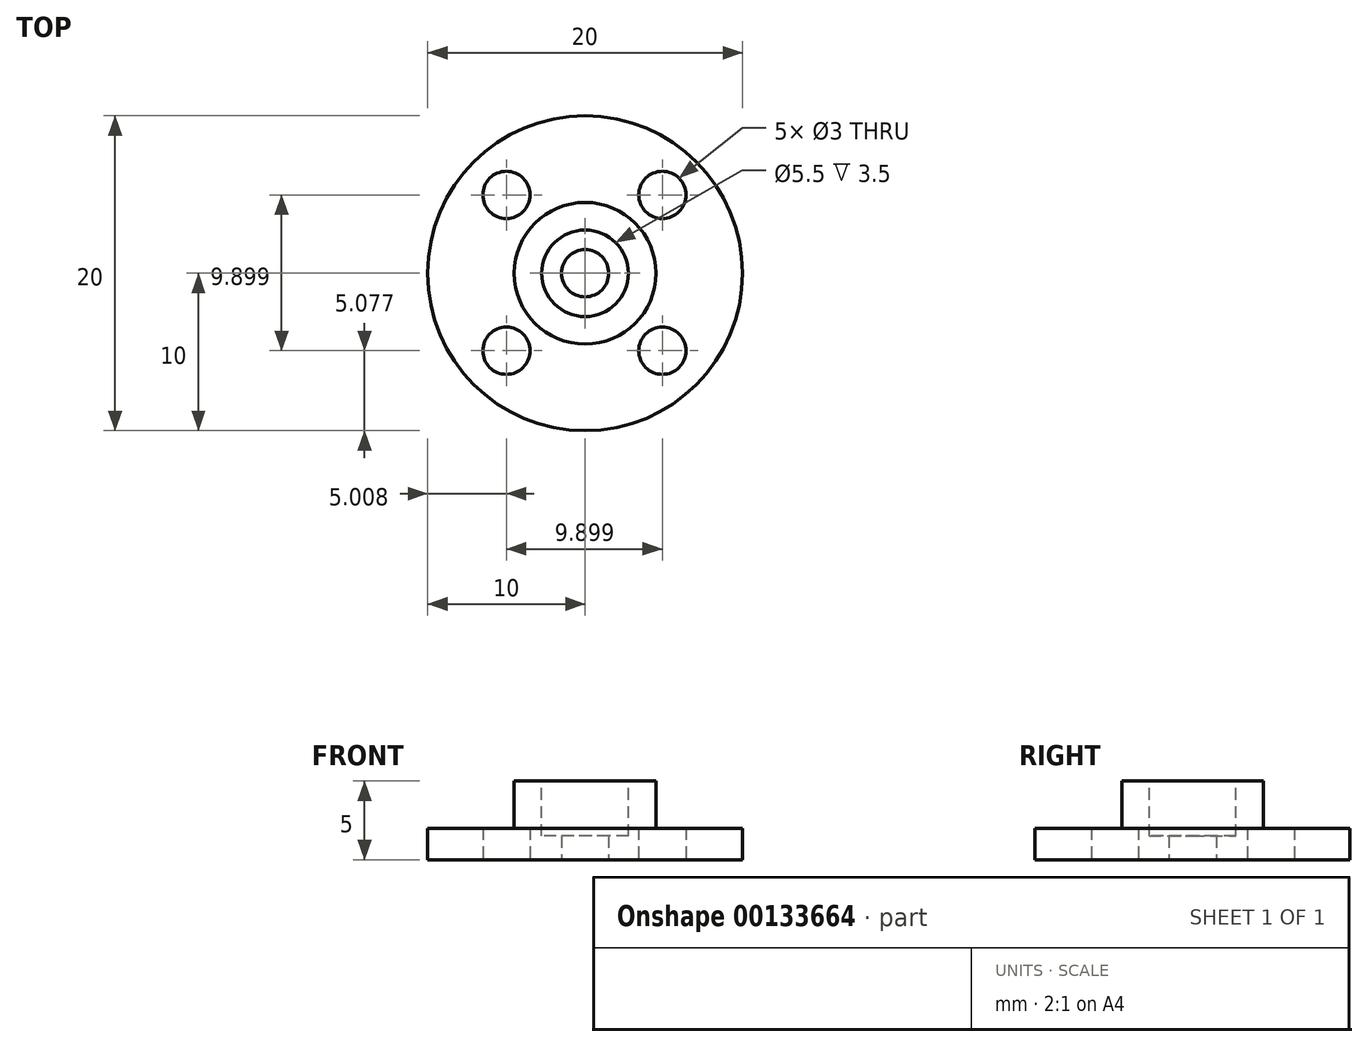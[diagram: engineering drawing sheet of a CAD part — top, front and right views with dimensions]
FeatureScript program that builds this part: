
annotation { "Feature Type Name" : "Feature", "Feature Type Description" : "" }
export const myFeature = defineFeature(function(context is Context, id is Id, definition is map)
    precondition{}
    {
        {
            var Q0;
            Q0=qCreatedBy(makeId("Top.planeOp"),FACE);
            var sketch = newSketch(context, id + "F0", { "sketchPlane" : qUnion([Q0])});
            skCircle(sketch, "E0", {"center": v(0, 0) * mm, "radius": 10 * mm});
            skCircle(sketch, "E1", {"center": v(0, 0) * mm, "radius": 1.5 * mm});
            skLineSegment(sketch, "E2.bottom", {"start": v(-5, -4.92) * mm, "end": v(4.9, -4.92) * mm, "construction": true});
            skLineSegment(sketch, "E2.top", {"start": v(-5, 4.98) * mm, "end": v(4.9, 4.98) * mm, "construction": true});
            skLineSegment(sketch, "E2.left", {"start": v(-5, -4.92) * mm, "end": v(-5, 4.98) * mm, "construction": true});
            skLineSegment(sketch, "E2.right", {"start": v(4.9, -4.92) * mm, "end": v(4.9, 4.98) * mm, "construction": true});
            skPoint(sketch, "E2.middle", {"position": v(-0.04, 0.03) * mm});
            skCircle(sketch, "E3", {"center": v(-5, 4.98) * mm, "radius": 1.5 * mm});
            skCircle(sketch, "E4", {"center": v(4.9, 4.98) * mm, "radius": 1.5 * mm});
            skCircle(sketch, "E5", {"center": v(4.9, -4.92) * mm, "radius": 1.5 * mm});
            skCircle(sketch, "E6", {"center": v(-5, -4.92) * mm, "radius": 1.5 * mm});
            skSolve(sketch);
        }
        {
            var Q0;
            Q0=makeQuery(id+"F0.imprint","IMPRINT",FACE,{"disambiguationData":[TD([[makeQuery(id+"F0.imprint","IMPRINT",EDGE,{"derivedFrom":sQuery(id+"F0.wireOp",EDGE,"E0")}),1.0]])]});
            extrude(context, id + "F1", {"entities" : qUnion([Q0]), "depth" : 2 * mm, "offsetDistance" : 25 * mm});
        }
        {
            var Q0;
            Q0=makeQuery(id+"F1.opExtrude","CAP_FACE",FACE,{"disambiguationData":[OSD([sQuery(id+"F0.wireOp",EDGE,"E0"),sQuery(id+"F0.wireOp",EDGE,"E1"),sQuery(id+"F0.wireOp",EDGE,"E3"),sQuery(id+"F0.wireOp",EDGE,"E4"),sQuery(id+"F0.wireOp",EDGE,"E5"),sQuery(id+"F0.wireOp",EDGE,"E6")])],"isStart":false});
            var sketch = newSketch(context, id + "F2", { "sketchPlane" : qUnion([Q0])});
            skSolve(sketch);
        }
        {
            var Q0;
            Q0=makeQuery(id+"F2.imprint","IMPRINT",FACE,{"disambiguationData":[TD([[makeQuery(id+"F2.imprint","IMPRINT",EDGE,{"derivedFrom":makeQuery(id+"F1.opExtrude","CAP_EDGE",EDGE,{"disambiguationData":[OSD([sQuery(id+"F0.wireOp",EDGE,"E0")])],"isStart":false})}),1.0]])]});
            var sketch = newSketch(context, id + "F3", { "sketchPlane" : qUnion([Q0])});
            skCircle(sketch, "E7", {"center": v(0, 0) * mm, "radius": 4.5 * mm});
            skCircle(sketch, "E8", {"center": v(0, 0) * mm, "radius": 2.75 * mm});
            skSolve(sketch);
        }
        {
            var Q0;
            Q0=makeQuery(id+"F3.imprint","IMPRINT",FACE,{"disambiguationData":[TD([[makeQuery(id+"F3.imprint","IMPRINT",EDGE,{"derivedFrom":sQuery(id+"F3.wireOp",EDGE,"E8")}),1.0]])]});
            extrude(context, id + "F4", {"entities" : qUnion([Q0]), "operationType" : NewBodyOperationType.REMOVE, "oppositeDirection" : true, "depth" : .5 * mm, "offsetDistance" : 25 * mm});
        }
        {
            var Q0;
            Q0=makeQuery(id+"F3.imprint","IMPRINT",FACE,{"disambiguationData":[TD([[makeQuery(id+"F3.imprint","IMPRINT",EDGE,{"derivedFrom":sQuery(id+"F3.wireOp",EDGE,"E7")}),1.0]])]});
            extrude(context, id + "F5", {"entities" : qUnion([Q0]), "operationType" : NewBodyOperationType.ADD, "depth" : 3 * mm, "offsetDistance" : 25 * mm});
        }
    });
